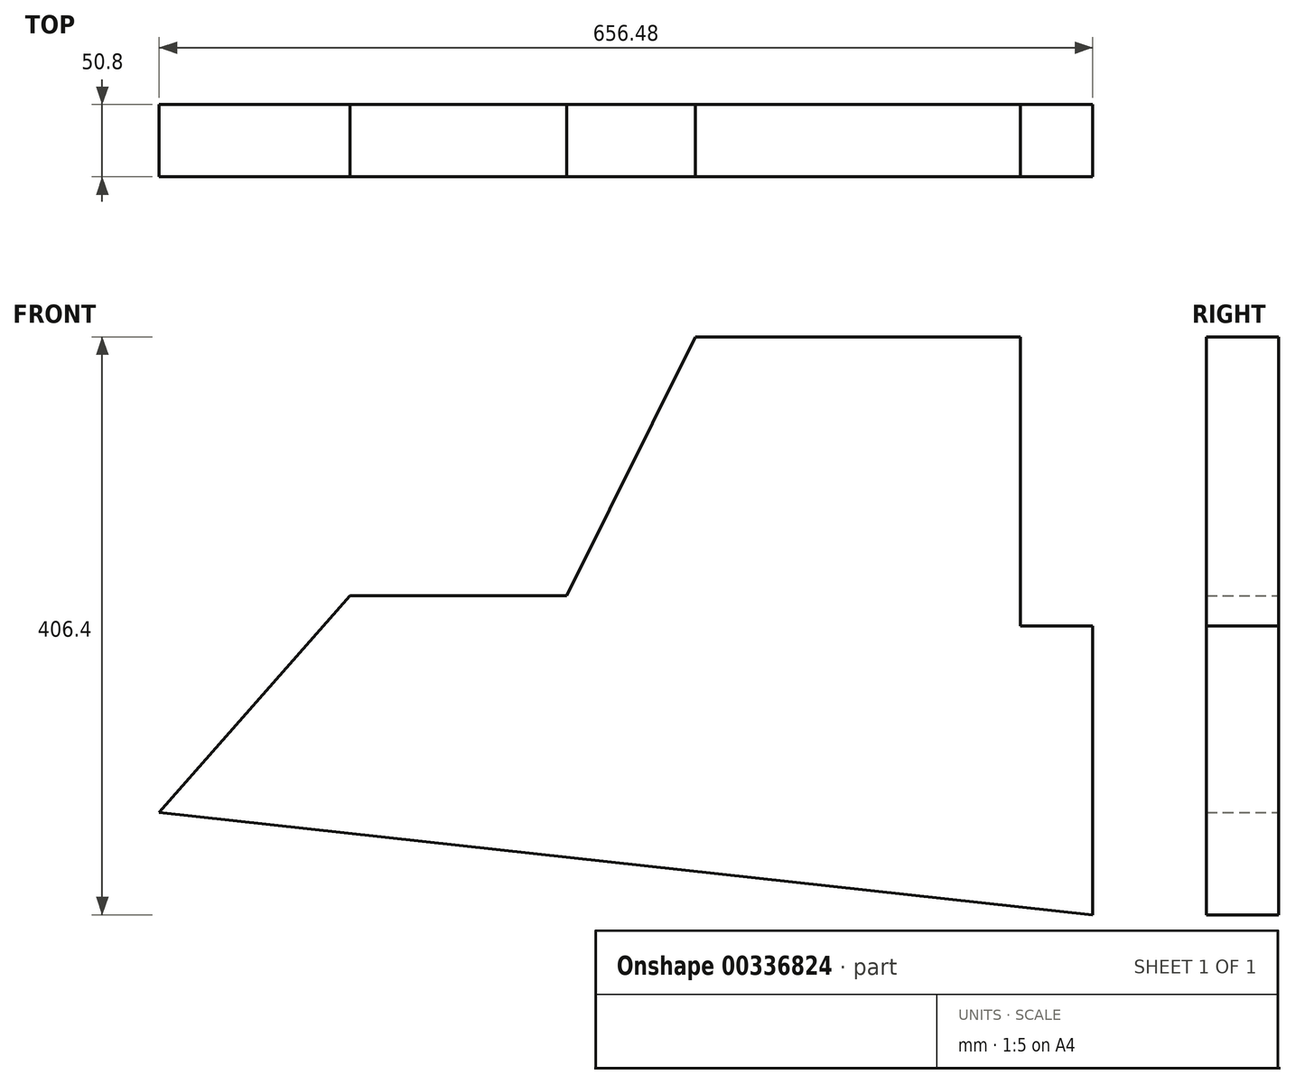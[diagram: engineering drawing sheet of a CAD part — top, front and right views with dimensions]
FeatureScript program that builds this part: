
annotation { "Feature Type Name" : "Feature", "Feature Type Description" : "" }
export const myFeature = defineFeature(function(context is Context, id is Id, definition is map)
    precondition{}
    {
        {
            var Q0;
            Q0=qCreatedBy(makeId("Front.planeOp"),FACE);
            var sketch = newSketch(context, id + "F0", { "sketchPlane" : qUnion([Q0])});
            skLineSegment(sketch, "E0", {"start": v(381.31, -71.85) * mm, "end": v(381.31, 131.35) * mm});
            skLineSegment(sketch, "E1", {"start": v(381.31, 131.35) * mm, "end": v(330.51, 131.35) * mm});
            skLineSegment(sketch, "E2", {"start": v(330.51, 131.35) * mm, "end": v(330.51, 334.55) * mm});
            skLineSegment(sketch, "E3", {"start": v(330.51, 334.55) * mm, "end": v(101.91, 334.55) * mm});
            skLineSegment(sketch, "E4", {"start": v(101.91, 334.55) * mm, "end": v(11.37, 152.63) * mm});
            skLineSegment(sketch, "E5", {"start": v(11.37, 152.63) * mm, "end": v(-141.03, 152.63) * mm});
            skLineSegment(sketch, "E6", {"start": v(-141.03, 152.63) * mm, "end": v(-275.17, 0) * mm});
            skLineSegment(sketch, "E7", {"start": v(-275.17, 0) * mm, "end": v(381.31, -71.85) * mm});
            skSolve(sketch);
        }
        {
            var Q0;
            Q0=makeQuery(id+"F0.imprint","IMPRINT",FACE,{"disambiguationData":[TD([[makeQuery(id+"F0.imprint","IMPRINT",EDGE,{"derivedFrom":sQuery(id+"F0.wireOp",EDGE,"E0")}),1.0]])]});
            extrude(context, id + "F1", {"entities" : qUnion([Q0]), "depth" : 50.8 * mm});
        }
    });
